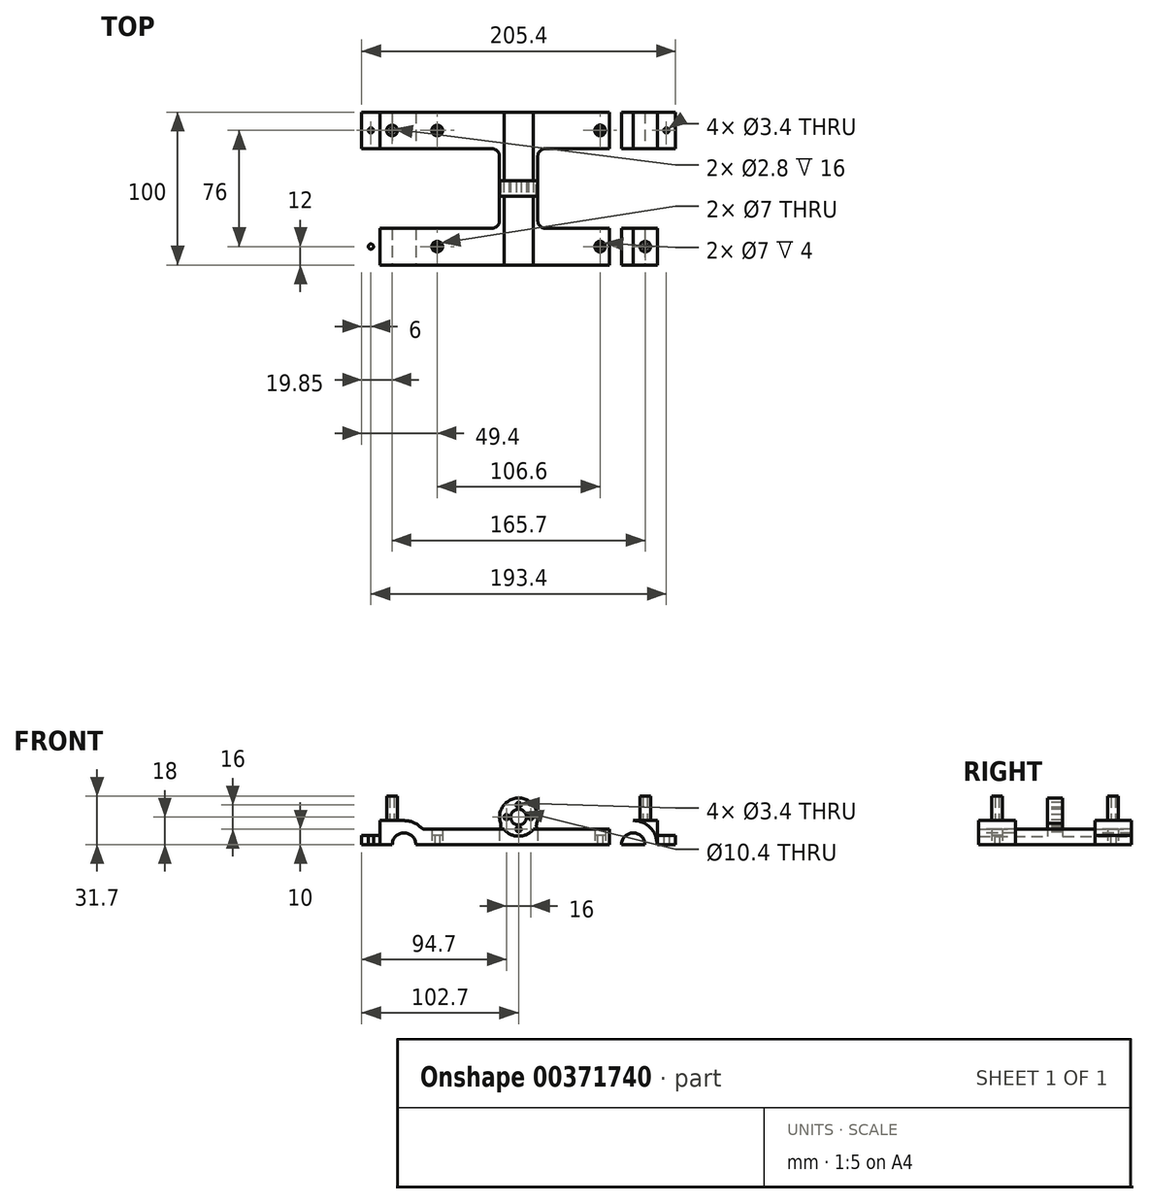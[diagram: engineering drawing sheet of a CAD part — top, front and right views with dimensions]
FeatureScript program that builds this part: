
annotation { "Feature Type Name" : "Feature", "Feature Type Description" : "" }
export const myFeature = defineFeature(function(context is Context, id is Id, definition is map)
    precondition{}
    {
        {
            var Q0;
            Q0=qCreatedBy(makeId("Top.planeOp"),FACE);
            var sketch = newSketch(context, id + "F0", { "sketchPlane" : qUnion([Q0])});
            skLineSegment(sketch, "E0", {"start": v(0, 0) * mm, "end": v(0, 50) * mm, "construction": true});
            skLineSegment(sketch, "E1", {"start": v(0, 0) * mm, "end": v(0, -50) * mm, "construction": true});
            skLineSegment(sketch, "E2", {"start": v(0, 50) * mm, "end": v(-59.3, 50) * mm});
            skLineSegment(sketch, "E3", {"start": v(-59.3, 50) * mm, "end": v(-59.3, 26) * mm});
            skLineSegment(sketch, "E4.bottom", {"start": v(-59.3, 26) * mm, "end": v(-90.7, 26) * mm});
            skLineSegment(sketch, "E4.top", {"start": v(-59.3, 50) * mm, "end": v(-90.7, 50) * mm});
            skLineSegment(sketch, "E4.left", {"start": v(-59.3, 26) * mm, "end": v(-59.3, 50) * mm});
            skLineSegment(sketch, "E4.right", {"start": v(-90.7, 26) * mm, "end": v(-90.7, 50) * mm});
            skLineSegment(sketch, "E5", {"start": v(-59.3, 26) * mm, "end": v(-12.5, 26) * mm});
            skLineSegment(sketch, "E6", {"start": v(0, 0) * mm, "end": v(-12.5, 0) * mm, "construction": true});
            skLineSegment(sketch, "E7", {"start": v(-12.5, 0) * mm, "end": v(-12.5, 26) * mm});
            skLineSegment(sketch, "E8.MirrorCS", {"start": v(59.3, 50) * mm, "end": v(90.7, 50) * mm});
            skLineSegment(sketch, "E9.MirrorCS", {"start": v(90.7, 26) * mm, "end": v(90.7, 50) * mm});
            skLineSegment(sketch, "E10.MirrorCS", {"start": v(59.3, 26) * mm, "end": v(90.7, 26) * mm});
            skLineSegment(sketch, "E11.MirrorCS", {"start": v(59.3, 26) * mm, "end": v(59.3, 50) * mm});
            skLineSegment(sketch, "E12.MirrorCS", {"start": v(59.3, 26) * mm, "end": v(12.5, 26) * mm});
            skLineSegment(sketch, "E13.MirrorCS", {"start": v(0, 50) * mm, "end": v(59.3, 50) * mm});
            skLineSegment(sketch, "E14.MirrorCS", {"start": v(12.5, 0) * mm, "end": v(12.5, 26) * mm});
            skLineSegment(sketch, "E15.MirrorCS", {"start": v(-12.5, 0) * mm, "end": v(-12.5, -26) * mm});
            skLineSegment(sketch, "E16.MirrorCS", {"start": v(-59.3, -26) * mm, "end": v(-12.5, -26) * mm});
            skLineSegment(sketch, "E17.MirrorCS", {"start": v(-59.3, -26) * mm, "end": v(-90.7, -26) * mm});
            skLineSegment(sketch, "E18.MirrorCS", {"start": v(-90.7, -26) * mm, "end": v(-90.7, -50) * mm});
            skLineSegment(sketch, "E19.MirrorCS", {"start": v(-59.3, -50) * mm, "end": v(-90.7, -50) * mm});
            skLineSegment(sketch, "E20.MirrorCS", {"start": v(-59.3, -26) * mm, "end": v(-59.3, -50) * mm});
            skLineSegment(sketch, "E21.MirrorCS", {"start": v(0, -50) * mm, "end": v(-59.3, -50) * mm});
            skLineSegment(sketch, "E22.MirrorCS", {"start": v(0, -50) * mm, "end": v(59.3, -50) * mm});
            skLineSegment(sketch, "E23.MirrorCS", {"start": v(59.3, -26) * mm, "end": v(12.5, -26) * mm});
            skLineSegment(sketch, "E24.MirrorCS", {"start": v(12.5, 0) * mm, "end": v(12.5, -26) * mm});
            skLineSegment(sketch, "E25.MirrorCS", {"start": v(59.3, -26) * mm, "end": v(90.7, -26) * mm});
            skLineSegment(sketch, "E26.MirrorCS", {"start": v(59.3, -26) * mm, "end": v(59.3, -50) * mm});
            skLineSegment(sketch, "E27.MirrorCS", {"start": v(59.3, -50) * mm, "end": v(90.7, -50) * mm});
            skLineSegment(sketch, "E28.MirrorCS", {"start": v(90.7, -26) * mm, "end": v(90.7, -50) * mm});
            skLineSegment(sketch, "E29.bottom", {"start": v(-12.5, 5) * mm, "end": v(12.5, 5) * mm});
            skLineSegment(sketch, "E29.top", {"start": v(-12.5, -5) * mm, "end": v(12.5, -5) * mm});
            skLineSegment(sketch, "E29.left", {"start": v(-12.5, 5) * mm, "end": v(-12.5, -5) * mm});
            skLineSegment(sketch, "E29.right", {"start": v(12.5, 5) * mm, "end": v(12.5, -5) * mm});
            skPoint(sketch, "E29.middle", {"position": v(0, 0) * mm});
            skLineSegment(sketch, "E30.bottom", {"start": v(-90.7, 50) * mm, "end": v(-99.7, 50) * mm});
            skLineSegment(sketch, "E30.top", {"start": v(-90.7, 26) * mm, "end": v(-99.7, 26) * mm});
            skLineSegment(sketch, "E30.left", {"start": v(-90.7, 50) * mm, "end": v(-90.7, 26) * mm});
            skCircle(sketch, "E31", {"center": v(-96.7, 38) * mm, "radius": 1.7 * mm});
            skPoint(sketch, "E31.centerSnap0", {"position": v(-90.7, 38) * mm});
            skPoint(sketch, "E31.centerSnap1", {"position": v(-96.7, 50) * mm});
            skLineSegment(sketch, "E32.MirrorCS", {"start": v(90.7, 50) * mm, "end": v(99.7, 50) * mm});
            skLineSegment(sketch, "E33.MirrorCS", {"start": v(90.7, 26) * mm, "end": v(99.7, 26) * mm});
            skLineSegment(sketch, "E34.MirrorCS", {"start": v(90.7, 50) * mm, "end": v(90.7, 26) * mm});
            skCircle(sketch, "E35.MirrorC", {"center": v(96.7, 38) * mm, "radius": 1.7 * mm});
            skCircle(sketch, "E36.MirrorC", {"center": v(-96.7, -38) * mm, "radius": 1.7 * mm});
            skLineSegment(sketch, "E37.MirrorCS", {"start": v(-90.7, -50) * mm, "end": v(-90.7, -26) * mm});
            skLineSegment(sketch, "E38.MirrorCS", {"start": v(-90.7, -50) * mm, "end": v(-99.7, -50) * mm});
            skLineSegment(sketch, "E39.MirrorCS", {"start": v(-90.7, -26) * mm, "end": v(-99.7, -26) * mm});
            skLineSegment(sketch, "E40.MirrorCS", {"start": v(90.7, -50) * mm, "end": v(90.7, -26) * mm});
            skLineSegment(sketch, "E41.MirrorCS", {"start": v(90.7, -50) * mm, "end": v(99.7, -50) * mm});
            skLineSegment(sketch, "E42.MirrorCS", {"start": v(90.7, -26) * mm, "end": v(99.7, -26) * mm});
            skCircle(sketch, "E43.MirrorC", {"center": v(96.7, -38) * mm, "radius": 1.7 * mm});
            skLineSegment(sketch, "E44", {"start": v(-59.3, 38) * mm, "end": v(-53.3, 38) * mm, "construction": true});
            skCircle(sketch, "E45", {"center": v(-53.3, 38) * mm, "radius": 1.7 * mm});
            skCircle(sketch, "E46.MirrorC", {"center": v(53.3, 38) * mm, "radius": 1.7 * mm});
            skCircle(sketch, "E47.MirrorC", {"center": v(-53.3, -38) * mm, "radius": 1.7 * mm});
            skCircle(sketch, "E48.MirrorC", {"center": v(53.3, -38) * mm, "radius": 1.7 * mm});
            skCircle(sketch, "E49", {"center": v(-53.3, 38) * mm, "radius": 3.5 * mm});
            skCircle(sketch, "E50.MirrorC", {"center": v(53.3, 38) * mm, "radius": 3.5 * mm});
            skCircle(sketch, "E51.MirrorC", {"center": v(-53.3, -38) * mm, "radius": 3.5 * mm});
            skCircle(sketch, "E52.MirrorC", {"center": v(53.3, -38) * mm, "radius": 3.5 * mm});
            skLineSegment(sketch, "E53", {"start": v(-12.5, 0) * mm, "end": v(-60.78, 0) * mm, "construction": true});
            skLineSegment(sketch, "E54", {"start": v(-96.7, -38) * mm, "end": v(-90.7, -38) * mm, "construction": true});
            skLineSegment(sketch, "E55", {"start": v(-96.7, 38) * mm, "end": v(-90.7, 38) * mm, "construction": true});
            skPoint(sketch, "E56.orphan", {"position": v(-102.7, 26) * mm});
            skPoint(sketch, "E57.orphan", {"position": v(-102.7, 50) * mm});
            skPoint(sketch, "E58.MirrorCS.end.orphan", {"position": v(-102.7, -26) * mm});
            skPoint(sketch, "E58.MirrorCS.start.orphan", {"position": v(-102.7, -50) * mm});
            skPoint(sketch, "E59.orphan", {"position": v(102.7, -26) * mm});
            skPoint(sketch, "E60.MirrorCS.start.orphan", {"position": v(102.7, -50) * mm});
            skPoint(sketch, "E61.orphan", {"position": v(102.7, 26) * mm});
            skPoint(sketch, "E62.MirrorCS.start.orphan", {"position": v(102.7, 50) * mm});
            skLineSegment(sketch, "E63", {"start": v(-102.7, 50) * mm, "end": v(-99.7, 50) * mm});
            skLineSegment(sketch, "E64", {"start": v(-102.7, 50) * mm, "end": v(-102.7, 26) * mm});
            skLineSegment(sketch, "E65", {"start": v(-102.7, 26) * mm, "end": v(-99.7, 26) * mm});
            skLineSegment(sketch, "E66.MirrorCS", {"start": v(102.7, 50) * mm, "end": v(102.7, 26) * mm});
            skLineSegment(sketch, "E67.MirrorCS", {"start": v(102.7, 26) * mm, "end": v(99.7, 26) * mm});
            skLineSegment(sketch, "E68.MirrorCS", {"start": v(102.7, 50) * mm, "end": v(99.7, 50) * mm});
            skLineSegment(sketch, "E69.MirrorCS", {"start": v(102.7, -26) * mm, "end": v(99.7, -26) * mm});
            skLineSegment(sketch, "E70.MirrorCS", {"start": v(102.7, -50) * mm, "end": v(102.7, -26) * mm});
            skLineSegment(sketch, "E71.MirrorCS", {"start": v(102.7, -50) * mm, "end": v(99.7, -50) * mm});
            skLineSegment(sketch, "E72.MirrorCS", {"start": v(-102.7, -50) * mm, "end": v(-99.7, -50) * mm});
            skLineSegment(sketch, "E73.MirrorCS", {"start": v(-102.7, -50) * mm, "end": v(-102.7, -26) * mm});
            skLineSegment(sketch, "E74.MirrorCS", {"start": v(-102.7, -26) * mm, "end": v(-99.7, -26) * mm});
            skSolve(sketch);
        }
        {
            var Q0;
            Q0=makeQuery(id+"F0.imprint","IMPRINT",FACE,{"disambiguationData":[TD([[makeQuery(id+"F0.imprint","IMPRINT",EDGE,{"derivedFrom":sQuery(id+"F0.wireOp",EDGE,"E2")}),1.0]])]});
            var Q1;
            Q1=makeQuery(id+"F0.imprint","IMPRINT",FACE,{"disambiguationData":[TD([[makeQuery(id+"F0.imprint","IMPRINT",EDGE,{"derivedFrom":sQuery(id+"F0.wireOp",EDGE,"E15.MirrorCS")}),1.0]])]});
            extrude(context, id + "F1", {"entities" : qUnion([Q0, Q1]), "depth" : 10 * mm});
        }
        {
            var Q0;
            Q0=makeQuery(id+"F0.imprint","IMPRINT",FACE,{"disambiguationData":[TD([[makeQuery(id+"F0.imprint","IMPRINT",EDGE,{"derivedFrom":sQuery(id+"F0.wireOp",EDGE,"E17.MirrorCS")}),1.0]])]});
            var Q1;
            Q1=makeQuery(id+"F0.imprint","IMPRINT",FACE,{"disambiguationData":[TD([[makeQuery(id+"F0.imprint","IMPRINT",EDGE,{"derivedFrom":sQuery(id+"F0.wireOp",EDGE,"E4.bottom")}),-1.0]])]});
            var Q2;
            Q2=makeQuery(id+"F0.imprint","IMPRINT",FACE,{"disambiguationData":[TD([[makeQuery(id+"F0.imprint","IMPRINT",EDGE,{"derivedFrom":sQuery(id+"F0.wireOp",EDGE,"E8.MirrorCS")}),-1.0]])]});
            var Q3;
            Q3=makeQuery(id+"F0.imprint","IMPRINT",FACE,{"disambiguationData":[TD([[makeQuery(id+"F0.imprint","IMPRINT",EDGE,{"derivedFrom":sQuery(id+"F0.wireOp",EDGE,"E25.MirrorCS")}),-1.0]])]});
            extrude(context, id + "F2", {"entities" : qUnion([Q0, Q1, Q2, Q3]), "depth" : 15.7 * mm});
        }
        {
            var Q0;
            Q0=makeQuery(id+"F0.imprint","IMPRINT",FACE,{"disambiguationData":[TD([[makeQuery(id+"F0.imprint","IMPRINT",EDGE,{"derivedFrom":sQuery(id+"F0.wireOp",EDGE,"E29.bottom")}),-1.0]])]});
            extrude(context, id + "F3", {"entities" : qUnion([Q0]), "depth" : 30.5 * mm});
        }
        {
            var Q0;
            Q0=makeQuery(id+"F2.opExtrude","SWEPT_BODY",BODY,{"disambiguationData":[OSD([sQuery(id+"F0.wireOp",EDGE,"E25.MirrorCS"),sQuery(id+"F0.wireOp",EDGE,"E26.MirrorCS"),sQuery(id+"F0.wireOp",EDGE,"E27.MirrorCS"),sQuery(id+"F0.wireOp",EDGE,"E28.MirrorCS")])]});
            var Q1;
            Q1=makeQuery(id+"F2.opExtrude","SWEPT_BODY",BODY,{"disambiguationData":[OSD([sQuery(id+"F0.wireOp",EDGE,"E4.bottom"),sQuery(id+"F0.wireOp",EDGE,"E4.top"),sQuery(id+"F0.wireOp",EDGE,"E4.left"),sQuery(id+"F0.wireOp",EDGE,"E4.right")])]});
            var Q2;
            Q2=makeQuery(id+"F2.opExtrude","SWEPT_BODY",BODY,{"disambiguationData":[OSD([sQuery(id+"F0.wireOp",EDGE,"E17.MirrorCS"),sQuery(id+"F0.wireOp",EDGE,"E18.MirrorCS"),sQuery(id+"F0.wireOp",EDGE,"E19.MirrorCS"),sQuery(id+"F0.wireOp",EDGE,"E20.MirrorCS")])]});
            var Q3;
            Q3=makeQuery(id+"F1.opExtrude","SWEPT_BODY",BODY,{"disambiguationData":[OSD([sQuery(id+"F0.wireOp",EDGE,"E2"),sQuery(id+"F0.wireOp",EDGE,"E4.left"),sQuery(id+"F0.wireOp",EDGE,"E5"),sQuery(id+"F0.wireOp",EDGE,"E7"),sQuery(id+"F0.wireOp",EDGE,"E11.MirrorCS"),sQuery(id+"F0.wireOp",EDGE,"E12.MirrorCS"),sQuery(id+"F0.wireOp",EDGE,"E13.MirrorCS"),sQuery(id+"F0.wireOp",EDGE,"E14.MirrorCS"),sQuery(id+"F0.wireOp",EDGE,"E29.bottom")])]});
            var Q4;
            Q4=makeQuery(id+"F1.opExtrude","SWEPT_BODY",BODY,{"disambiguationData":[OSD([sQuery(id+"F0.wireOp",EDGE,"E15.MirrorCS"),sQuery(id+"F0.wireOp",EDGE,"E16.MirrorCS"),sQuery(id+"F0.wireOp",EDGE,"E20.MirrorCS"),sQuery(id+"F0.wireOp",EDGE,"E21.MirrorCS"),sQuery(id+"F0.wireOp",EDGE,"E22.MirrorCS"),sQuery(id+"F0.wireOp",EDGE,"E23.MirrorCS"),sQuery(id+"F0.wireOp",EDGE,"E24.MirrorCS"),sQuery(id+"F0.wireOp",EDGE,"E26.MirrorCS"),sQuery(id+"F0.wireOp",EDGE,"E29.top")])]});
            var Q5;
            Q5=makeQuery(id+"F3.opExtrude","SWEPT_BODY",BODY,{"disambiguationData":[OSD([sQuery(id+"F0.wireOp",EDGE,"E29.bottom"),sQuery(id+"F0.wireOp",EDGE,"E29.top"),sQuery(id+"F0.wireOp",EDGE,"E29.left"),sQuery(id+"F0.wireOp",EDGE,"E29.right")])]});
            var Q6;
            Q6=makeQuery(id+"F2.opExtrude","SWEPT_BODY",BODY,{"disambiguationData":[OSD([sQuery(id+"F0.wireOp",EDGE,"E8.MirrorCS"),sQuery(id+"F0.wireOp",EDGE,"E9.MirrorCS"),sQuery(id+"F0.wireOp",EDGE,"E10.MirrorCS"),sQuery(id+"F0.wireOp",EDGE,"E11.MirrorCS")])]});
            booleanBodies(context, id + "F4", {"operationType" : BooleanOperationType.UNION, "tools" : qUnion([Q0, Q1, Q2, Q3, Q4, Q5, Q6])});
        }
        {
            var Q0;
            Q0=makeQuery(id+"F4.opBoolean","MERGE",FACE,{"derivedFrom":[makeQuery(id+"F1.opExtrude","SWEPT_FACE",FACE,{"disambiguationData":[OSD([sQuery(id+"F0.wireOp",EDGE,"E21.MirrorCS"),sQuery(id+"F0.wireOp",EDGE,"E22.MirrorCS")])]}),makeQuery(id+"F2.opExtrude","SWEPT_FACE",FACE,{"disambiguationData":[OSD([sQuery(id+"F0.wireOp",EDGE,"E19.MirrorCS")])]}),makeQuery(id+"F2.opExtrude","SWEPT_FACE",FACE,{"disambiguationData":[OSD([sQuery(id+"F0.wireOp",EDGE,"E27.MirrorCS")])]})]});
            var sketch = newSketch(context, id + "F5", { "sketchPlane" : qUnion([Q0])});
            skLineSegment(sketch, "E75", {"start": v(-75, 15.7) * mm, "end": v(-75, 0) * mm, "construction": true});
            skArc(sketch, "E76", {"start": v(-64.07, 11.27) * mm, "mid": v(-81.12, 14.46) * mm, "end": v(-90.7, 0) * mm});
            skArc(sketch, "E77", {"start": v(-67.3, 0) * mm, "mid": v(-75, 7.7) * mm, "end": v(-82.7, 0) * mm});
            skLineSegment(sketch, "E78", {"start": v(-82.7, 0) * mm, "end": v(-90.7, 0) * mm});
            skLineSegment(sketch, "E79", {"start": v(-67.3, 0) * mm, "end": v(-59.3, 0) * mm});
            skLineSegment(sketch, "E80", {"start": v(0, 0) * mm, "end": v(0, 35.4) * mm, "construction": true});
            skPoint(sketch, "E80.endSnap0", {"position": v(0, 0) * mm});
            skArc(sketch, "E81.MirrorCS", {"start": v(67.3, 0) * mm, "mid": v(75, 7.7) * mm, "end": v(82.7, 0) * mm});
            skLineSegment(sketch, "E82.MirrorCS", {"start": v(82.7, 0) * mm, "end": v(90.7, 0) * mm});
            skArc(sketch, "E83.MirrorCS", {"start": v(64.07, 11.27) * mm, "mid": v(81.12, 14.46) * mm, "end": v(90.7, 0) * mm});
            skLineSegment(sketch, "E84.MirrorCS", {"start": v(67.3, 0) * mm, "end": v(59.3, 0) * mm});
            skLineSegment(sketch, "E85", {"start": v(-59.3, 0) * mm, "end": v(-59.3, 15.7) * mm});
            skLineSegment(sketch, "E86", {"start": v(-59.3, 15.7) * mm, "end": v(-75, 15.7) * mm});
            skLineSegment(sketch, "E87.MirrorCS", {"start": v(59.3, 15.7) * mm, "end": v(75, 15.7) * mm});
            skLineSegment(sketch, "E88.MirrorCS", {"start": v(59.3, 0) * mm, "end": v(59.3, 15.7) * mm});
            skLineSegment(sketch, "E89", {"start": v(-59.3, 10) * mm, "end": v(-60.94, 10) * mm});
            skPoint(sketch, "E90.newPointA", {"position": v(-59.3, 0) * mm});
            skArc(sketch, "E90.filletArc", {"start": v(-64.07, 11.27) * mm, "mid": v(-62.63, 10.33) * mm, "end": v(-60.94, 10) * mm});
            skLineSegment(sketch, "E91", {"start": v(59.3, 10) * mm, "end": v(60.94, 10) * mm});
            skPoint(sketch, "E92.newPointB", {"position": v(59.3, 0) * mm});
            skArc(sketch, "E92.filletArc", {"start": v(60.94, 10) * mm, "mid": v(62.63, 10.33) * mm, "end": v(64.07, 11.27) * mm});
            skSolve(sketch);
        }
        {
            var Q0;
            {var subQ6=sQuery(id+"F5.wireOp",EDGE,"E87.MirrorCS");Q0=makeQuery(id+"F5.imprint","IMPRINT",FACE,{"disambiguationData":[TD([[makeQuery(id+"F5.imprint","IMPRINT",EDGE,{"derivedFrom":subQ6}),-1.0]])]});}
            var Q1;
            {var subQ0=sQuery(id+"F5.wireOp",EDGE,"8ee72258-81a3-4149-ab89-0d706ac254500.MirrorCS");Q1=makeQuery(id+"F5.imprint","IMPRINT",FACE,{"disambiguationData":[TD([[makeQuery(id+"F5.imprint","IMPRINT",EDGE,{"derivedFrom":subQ0}),-1.0]])]});}
            var Q2;
            {var subQ0=sQuery(id+"F5.wireOp",EDGE,"E81.MirrorCS");Q2=makeQuery(id+"F5.imprint","IMPRINT",FACE,{"disambiguationData":[TD([[makeQuery(id+"F5.imprint","IMPRINT",EDGE,{"derivedFrom":subQ0}),-1.0]])]});}
            var Q3;
            {var subQ0=sQuery(id+"F5.wireOp",EDGE,"2AFTPnqg-4Tv1-YmLw-YE9B-kkPoXeHdkq1D");Q3=makeQuery(id+"F5.imprint","IMPRINT",FACE,{"disambiguationData":[TD([[makeQuery(id+"F5.imprint","IMPRINT",EDGE,{"derivedFrom":subQ0}),1.0]])]});}
            var Q4;
            {var subQ6=sQuery(id+"F5.wireOp",EDGE,"E86");Q4=makeQuery(id+"F5.imprint","IMPRINT",FACE,{"disambiguationData":[TD([[makeQuery(id+"F5.imprint","IMPRINT",EDGE,{"derivedFrom":subQ6}),1.0]])]});}
            var Q5;
            {var subQ0=sQuery(id+"F5.wireOp",EDGE,"E77");Q5=makeQuery(id+"F5.imprint","IMPRINT",FACE,{"disambiguationData":[TD([[makeQuery(id+"F5.imprint","IMPRINT",EDGE,{"derivedFrom":subQ0}),1.0]])]});}
            extrude(context, id + "F6", {"entities" : qUnion([Q0, Q1, Q2, Q3, Q4, Q5]), "operationType" : NewBodyOperationType.REMOVE, "oppositeDirection" : true, "depth" : 100 * mm});
        }
        {
            var Q0;
            Q0=makeQuery(id+"F3.opExtrude","SWEPT_FACE",FACE,{"disambiguationData":[OSD([sQuery(id+"F0.wireOp",EDGE,"E29.top")])]});
            var sketch = newSketch(context, id + "F7", { "sketchPlane" : qUnion([Q0])});
            skLineSegment(sketch, "E93", {"start": v(0, 0) * mm, "end": v(0, 18) * mm, "construction": true});
            skFitSpline(sketch, "E94", {"points": [v(-11.82, 13.93) * mm, v(-11.66, 11.67) * mm, v(-12.5, 10) * mm], "startDerivative": vector(0.82, -4.52) * mm, "endDerivative": vector(-2.25, -3.32) * mm});
            skFitSpline(sketch, "E95.MirrorCS", {"points": [v(11.82, 13.93) * mm, v(11.66, 11.67) * mm, v(12.5, 10) * mm], "startDerivative": vector(-0.82, -4.52) * mm, "endDerivative": vector(2.25, -3.32) * mm});
            skCircle(sketch, "E96", {"center": v(0, 18) * mm, "radius": 5.2 * mm});
            skCircle(sketch, "E97", {"center": v(0, 18) * mm, "radius": 8 * mm, "construction": true});
            skArc(sketch, "E98", {"start": v(11.82, 13.93) * mm, "mid": v(0, 30.5) * mm, "end": v(-11.82, 13.93) * mm});
            skCircle(sketch, "E99", {"center": v(0, 26) * mm, "radius": 1.7 * mm});
            skCircle(sketch, "E100", {"center": v(8, 18) * mm, "radius": 1.7 * mm});
            skCircle(sketch, "E101", {"center": v(0, 10) * mm, "radius": 1.7 * mm});
            skCircle(sketch, "E102", {"center": v(-8, 18) * mm, "radius": 1.7 * mm});
            skLineSegment(sketch, "E103", {"start": v(-12.5, 10) * mm, "end": v(-9.6, 10) * mm});
            skLineSegment(sketch, "E104", {"start": v(12.5, 10) * mm, "end": v(9.6, 10) * mm});
            skArc(sketch, "E105.trimOffspring", {"start": v(-9.6, 10) * mm, "mid": v(0, 5.5) * mm, "end": v(9.6, 10) * mm});
            skSolve(sketch);
        }
        {
            var Q0;
            {var subQ0=sQuery(id+"F7.wireOp",EDGE,"E98");var subQ1=sQuery(id+"F0.wireOp",EDGE,"E29.top");var subQ2=makeQuery(id+"F3.opExtrude","CAP_EDGE",EDGE,{"disambiguationData":[OSD([subQ1])],"isStart":false});var subQ3=makeQuery(id+"F7.imprint","INTERSECT",VERTEX,{"derivedFrom":[subQ2,subQ0]});Q0=makeQuery(id+"F7.imprint","IMPRINT",FACE,{"disambiguationData":[TD([[makeQuery(id+"F7.imprint","IMPRINT",EDGE,{"disambiguationData":[TD([[subQ3,-1.0]])],"derivedFrom":subQ0}),-1.0]])]});}
            var Q1;
            {var subQ0=sQuery(id+"F7.wireOp",EDGE,"E98");var subQ1=sQuery(id+"F0.wireOp",EDGE,"E29.top");var subQ4=makeQuery(id+"F3.opExtrude","CAP_EDGE",EDGE,{"disambiguationData":[OSD([subQ1])],"isStart":false});var subQ5=makeQuery(id+"F7.imprint","INTERSECT",VERTEX,{"derivedFrom":[subQ4,subQ0]});Q1=makeQuery(id+"F7.imprint","IMPRINT",FACE,{"disambiguationData":[TD([[makeQuery(id+"F7.imprint","IMPRINT",EDGE,{"disambiguationData":[TD([[subQ5,1.0]])],"derivedFrom":subQ0}),-1.0]])]});}
            var Q2;
            {var subQ0=sQuery(id+"F7.wireOp",EDGE,"E94");Q2=makeQuery(id+"F7.imprint","IMPRINT",FACE,{"disambiguationData":[TD([[makeQuery(id+"F7.imprint","IMPRINT",EDGE,{"derivedFrom":subQ0}),-1.0]])]});}
            var Q3;
            {var subQ0=sQuery(id+"F7.wireOp",EDGE,"E95.MirrorCS");Q3=makeQuery(id+"F7.imprint","IMPRINT",FACE,{"disambiguationData":[TD([[makeQuery(id+"F7.imprint","IMPRINT",EDGE,{"derivedFrom":subQ0}),1.0]])]});}
            var Q4;
            Q4=makeQuery(id+"F7.imprint","IMPRINT",FACE,{"disambiguationData":[TD([[makeQuery(id+"F7.imprint","IMPRINT",EDGE,{"derivedFrom":sQuery(id+"F7.wireOp",EDGE,"E102")}),1.0]])]});
            var Q5;
            Q5=makeQuery(id+"F7.imprint","IMPRINT",FACE,{"disambiguationData":[TD([[makeQuery(id+"F7.imprint","IMPRINT",EDGE,{"derivedFrom":sQuery(id+"F7.wireOp",EDGE,"E99")}),1.0]])]});
            var Q6;
            Q6=makeQuery(id+"F7.imprint","IMPRINT",FACE,{"disambiguationData":[TD([[makeQuery(id+"F7.imprint","IMPRINT",EDGE,{"derivedFrom":sQuery(id+"F7.wireOp",EDGE,"E100")}),1.0]])]});
            var Q7;
            {var subQ0=sQuery(id+"F7.wireOp",EDGE,"E101");var subQ1=makeQuery(id+"F1.opExtrude","CAP_EDGE",EDGE,{"disambiguationData":[OSD([sQuery(id+"F0.wireOp",EDGE,"E29.top")])],"isStart":false});var subQ2=makeQuery(id+"F7.imprint","INTERSECT",VERTEX,{"disambiguationData":[OD(0.0)],"derivedFrom":[subQ1,subQ0]});Q7=makeQuery(id+"F7.imprint","IMPRINT",FACE,{"disambiguationData":[TD([[makeQuery(id+"F7.imprint","IMPRINT",EDGE,{"disambiguationData":[TD([[subQ2,1.0]])],"derivedFrom":subQ0}),1.0]])]});}
            var Q8;
            {var subQ0=sQuery(id+"F7.wireOp",EDGE,"E101");var subQ1=makeQuery(id+"F1.opExtrude","CAP_EDGE",EDGE,{"disambiguationData":[OSD([sQuery(id+"F0.wireOp",EDGE,"E29.top")])],"isStart":false});var subQ2=makeQuery(id+"F7.imprint","INTERSECT",VERTEX,{"disambiguationData":[OD(0.0)],"derivedFrom":[subQ1,subQ0]});Q8=makeQuery(id+"F7.imprint","IMPRINT",FACE,{"disambiguationData":[TD([[makeQuery(id+"F7.imprint","IMPRINT",EDGE,{"disambiguationData":[TD([[subQ2,-1.0]])],"derivedFrom":subQ0}),1.0]])]});}
            var Q9;
            Q9=makeQuery(id+"F7.imprint","IMPRINT",FACE,{"disambiguationData":[TD([[makeQuery(id+"F7.imprint","IMPRINT",EDGE,{"derivedFrom":sQuery(id+"F7.wireOp",EDGE,"E96")}),1.0]])]});
            extrude(context, id + "F8", {"entities" : qUnion([Q0, Q1, Q2, Q3, Q4, Q5, Q6, Q7, Q8, Q9]), "operationType" : NewBodyOperationType.REMOVE, "endBound" : BoundingType.SYMMETRIC, "oppositeDirection" : true, "depth" : 120 * mm});
        }
        {
            var Q0;
            {var subQ4=sQuery(id+"F7.wireOp",EDGE,"E105.trimOffspring");Q0=makeQuery(id+"F7.imprint","IMPRINT",FACE,{"disambiguationData":[TD([[makeQuery(id+"F7.imprint","IMPRINT",EDGE,{"derivedFrom":subQ4}),1.0]])]});}
            extrude(context, id + "F9", {"entities" : qUnion([Q0]), "operationType" : NewBodyOperationType.REMOVE, "depth" : 100 * mm});
        }
        {
            var Q0;
            {var subQ4=sQuery(id+"F7.wireOp",EDGE,"E105.trimOffspring");Q0=makeQuery(id+"F7.imprint","IMPRINT",FACE,{"disambiguationData":[TD([[makeQuery(id+"F7.imprint","IMPRINT",EDGE,{"derivedFrom":subQ4}),1.0]])]});}
            extrude(context, id + "F10", {"entities" : qUnion([Q0]), "operationType" : NewBodyOperationType.REMOVE, "oppositeDirection" : true, "depth" : 100 * mm});
        }
        {
            var Q0;
            {var subQ4=sQuery(id+"F7.wireOp",EDGE,"E105.trimOffspring");Q0=makeQuery(id+"F7.imprint","IMPRINT",FACE,{"disambiguationData":[TD([[makeQuery(id+"F7.imprint","IMPRINT",EDGE,{"derivedFrom":subQ4}),1.0]])]});}
            extrude(context, id + "F11", {"entities" : qUnion([Q0]), "operationType" : NewBodyOperationType.ADD, "oppositeDirection" : true, "depth" : 10 * mm});
        }
        {
            var Q0;
            Q0=makeQuery(id+"F1.opExtrude","SWEPT_EDGE",EDGE,{"disambiguationData":[OSD([sQuery(id+"F0.wireOp",EDGE,"E5"),sQuery(id+"F0.wireOp",EDGE,"E7")])]});
            var Q1;
            Q1=makeQuery(id+"F1.opExtrude","SWEPT_EDGE",EDGE,{"disambiguationData":[OSD([sQuery(id+"F0.wireOp",EDGE,"E12.MirrorCS"),sQuery(id+"F0.wireOp",EDGE,"E14.MirrorCS")])]});
            var Q2;
            Q2=makeQuery(id+"F1.opExtrude","SWEPT_EDGE",EDGE,{"disambiguationData":[OSD([sQuery(id+"F0.wireOp",EDGE,"E15.MirrorCS"),sQuery(id+"F0.wireOp",EDGE,"E16.MirrorCS")])]});
            var Q3;
            Q3=makeQuery(id+"F1.opExtrude","SWEPT_EDGE",EDGE,{"disambiguationData":[OSD([sQuery(id+"F0.wireOp",EDGE,"E23.MirrorCS"),sQuery(id+"F0.wireOp",EDGE,"E24.MirrorCS")])]});
            fillet(context, id + "F12", {"entities" : qUnion([Q0, Q1, Q2, Q3]), "radius" : 5 * mm, "tangentPropagation" : true, "allowEdgeOverflow" : false});
        }
        {
            var Q0;
            Q0=makeQuery(id+"F0.imprint","IMPRINT",FACE,{"disambiguationData":[TD([[makeQuery(id+"F0.imprint","IMPRINT",EDGE,{"derivedFrom":sQuery(id+"F0.wireOp",EDGE,"E30.bottom")}),1.0]])]});
            var Q1;
            Q1=makeQuery(id+"F0.imprint","IMPRINT",FACE,{"disambiguationData":[TD([[makeQuery(id+"F0.imprint","IMPRINT",EDGE,{"derivedFrom":sQuery(id+"F0.wireOp",EDGE,"E36.MirrorC")}),1.0]])]});
            var Q2;
            Q2=makeQuery(id+"F0.imprint","IMPRINT",FACE,{"disambiguationData":[TD([[makeQuery(id+"F0.imprint","IMPRINT",EDGE,{"derivedFrom":sQuery(id+"F0.wireOp",EDGE,"E40.MirrorCS")}),-1.0]])]});
            var Q3;
            Q3=makeQuery(id+"F0.imprint","IMPRINT",FACE,{"disambiguationData":[TD([[makeQuery(id+"F0.imprint","IMPRINT",EDGE,{"derivedFrom":sQuery(id+"F0.wireOp",EDGE,"E32.MirrorCS")}),-1.0]])]});
            extrude(context, id + "F13", {"entities" : qUnion([Q0, Q1, Q2, Q3]), "depth" : 6 * mm});
        }
        {
            var Q0;
            Q0=makeQuery(id+"F0.imprint","IMPRINT",FACE,{"disambiguationData":[TD([[makeQuery(id+"F0.imprint","IMPRINT",EDGE,{"derivedFrom":sQuery(id+"F0.wireOp",EDGE,"E45")}),-1.0]])]});
            var Q1;
            Q1=makeQuery(id+"F0.imprint","IMPRINT",FACE,{"disambiguationData":[TD([[makeQuery(id+"F0.imprint","IMPRINT",EDGE,{"derivedFrom":sQuery(id+"F0.wireOp",EDGE,"E46.MirrorC")}),1.0]])]});
            var Q2;
            Q2=makeQuery(id+"F0.imprint","IMPRINT",FACE,{"disambiguationData":[TD([[makeQuery(id+"F0.imprint","IMPRINT",EDGE,{"derivedFrom":sQuery(id+"F0.wireOp",EDGE,"E47.MirrorC")}),1.0]])]});
            var Q3;
            Q3=makeQuery(id+"F0.imprint","IMPRINT",FACE,{"disambiguationData":[TD([[makeQuery(id+"F0.imprint","IMPRINT",EDGE,{"derivedFrom":sQuery(id+"F0.wireOp",EDGE,"E48.MirrorC")}),-1.0]])]});
            extrude(context, id + "F14", {"entities" : qUnion([Q0, Q1, Q2, Q3]), "operationType" : NewBodyOperationType.ADD, "depth" : 6 * mm});
        }
        {
            var Q0;
            Q0=makeQuery(id+"F2.opExtrude","CAP_FACE",FACE,{"disambiguationData":[OSD([sQuery(id+"F0.wireOp",EDGE,"E4.bottom"),sQuery(id+"F0.wireOp",EDGE,"E4.top"),sQuery(id+"F0.wireOp",EDGE,"E4.left"),sQuery(id+"F0.wireOp",EDGE,"E30.left")])],"isStart":false});
            var sketch = newSketch(context, id + "F15", { "sketchPlane" : qUnion([Q0])});
            skLineSegment(sketch, "E106", {"start": v(-90.7, 50) * mm, "end": v(-75, 26) * mm, "construction": true});
            skLineSegment(sketch, "E107", {"start": v(-75, 50) * mm, "end": v(-90.7, 26) * mm, "construction": true});
            skCircle(sketch, "E108", {"center": v(-82.85, 38) * mm, "radius": 3.5 * mm});
            skLineSegment(sketch, "E109", {"start": v(0, 0) * mm, "end": v(0, 47.66) * mm, "construction": true});
            skLineSegment(sketch, "E110", {"start": v(0, 0) * mm, "end": v(-18.82, 0) * mm, "construction": true});
            skCircle(sketch, "E111.MirrorC", {"center": v(82.85, 38) * mm, "radius": 3.5 * mm});
            skCircle(sketch, "E112.MirrorC", {"center": v(-82.85, -38) * mm, "radius": 3.5 * mm});
            skCircle(sketch, "E113.MirrorC", {"center": v(82.85, -38) * mm, "radius": 3.5 * mm});
            skCircle(sketch, "E114", {"center": v(-82.85, -38) * mm, "radius": 1.4 * mm});
            skCircle(sketch, "E115.MirrorC", {"center": v(82.85, -38) * mm, "radius": 1.4 * mm});
            skCircle(sketch, "E116.MirrorC", {"center": v(-82.85, 38) * mm, "radius": 1.4 * mm});
            skCircle(sketch, "E117.MirrorC", {"center": v(82.85, 38) * mm, "radius": 1.4 * mm});
            skLineSegment(sketch, "E118", {"start": v(-18.82, 0) * mm, "end": v(-113.22, 0) * mm, "construction": true});
            skSolve(sketch);
        }
        {
            var Q0;
            Q0=makeQuery(id+"F15.imprint","IMPRINT",FACE,{"disambiguationData":[TD([[makeQuery(id+"F15.imprint","IMPRINT",EDGE,{"derivedFrom":sQuery(id+"F15.wireOp",EDGE,"E108")}),1.0]])]});
            var Q1;
            Q1=makeQuery(id+"F15.imprint","IMPRINT",FACE,{"disambiguationData":[TD([[makeQuery(id+"F15.imprint","IMPRINT",EDGE,{"derivedFrom":sQuery(id+"F15.wireOp",EDGE,"E111.MirrorC")}),-1.0]])]});
            var Q2;
            Q2=makeQuery(id+"F15.imprint","IMPRINT",FACE,{"disambiguationData":[TD([[makeQuery(id+"F15.imprint","IMPRINT",EDGE,{"derivedFrom":sQuery(id+"F15.wireOp",EDGE,"E113.MirrorC")}),1.0]])]});
            var Q3;
            Q3=makeQuery(id+"F15.imprint","IMPRINT",FACE,{"disambiguationData":[TD([[makeQuery(id+"F15.imprint","IMPRINT",EDGE,{"derivedFrom":sQuery(id+"F15.wireOp",EDGE,"E112.MirrorC")}),-1.0]])]});
            extrude(context, id + "F16", {"entities" : qUnion([Q0, Q1, Q2, Q3]), "operationType" : NewBodyOperationType.ADD, "depth" : 16 * mm});
        }
    });
